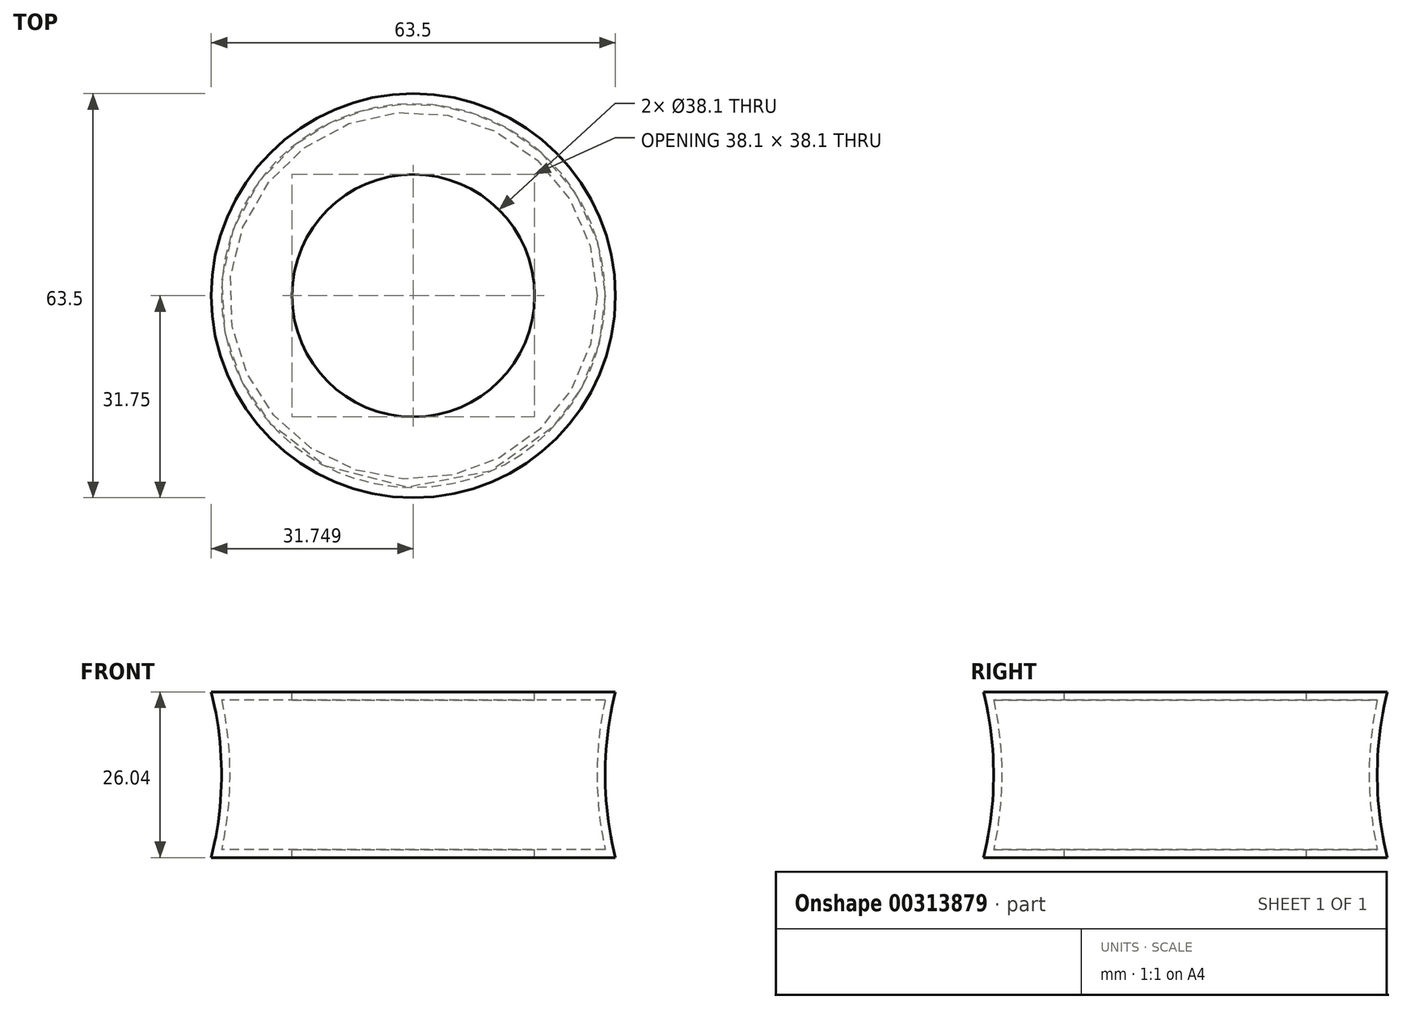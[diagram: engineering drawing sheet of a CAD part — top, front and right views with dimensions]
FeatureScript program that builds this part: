
annotation { "Feature Type Name" : "Feature", "Feature Type Description" : "" }
export const myFeature = defineFeature(function(context is Context, id is Id, definition is map)
    precondition{}
    {
        {
            var Q0;
            Q0=qCreatedBy(makeId("Front.planeOp"),FACE);
            var sketch = newSketch(context, id + "F0", { "sketchPlane" : qUnion([Q0])});
            skArc(sketch, "E0", {"start": v(-60.24, 12.57) * mm, "mid": v(-58.63, 25.6) * mm, "end": v(-60.24, 38.6) * mm});
            skLineSegment(sketch, "E1", {"start": v(-47.54, 38.6) * mm, "end": v(-47.54, 12.57) * mm});
            skLineSegment(sketch, "E2", {"start": v(-28.5, 38.32) * mm, "end": v(-28.5, 12.29) * mm});
            skArc(sketch, "E3", {"start": v(-47.54, 38.6) * mm, "mid": v(-53.89, 40.35) * mm, "end": v(-60.24, 38.6) * mm});
            skLineSegment(sketch, "E4", {"start": v(-60.24, 38.6) * mm, "end": v(-47.54, 38.6) * mm});
            skLineSegment(sketch, "E5", {"start": v(-60.24, 12.57) * mm, "end": v(-47.54, 12.57) * mm});
            skSolve(sketch);
        }
        {
            var Q0;
            Q0=makeQuery(id+"F0.imprint","IMPRINT",FACE,{"disambiguationData":[TD([[makeQuery(id+"F0.imprint","IMPRINT",EDGE,{"derivedFrom":sQuery(id+"F0.wireOp",EDGE,"E0")}),-1.0]])]});
            var Q1;
            Q1=sQuery(id+"F0.wireOp",EDGE,"E2");
            revolve(context, id + "F1", {"entities" : qUnion([Q0]), "axis" : qUnion([Q1]), "revolveType" : RevolveType.FULL});
        }
        {
            var Q0;
            Q0=makeQuery(id+"F1.opRevolve","SWEPT_FACE",FACE,{"disambiguationData":[OSD([sQuery(id+"F0.wireOp",EDGE,"E1")])]});
            shell(context, id + "F2", {"entities" : qUnion([Q0]), "thickness" : 1.27 * mm});
        }
    });
